# Revit family: A45743
name_source: partatom
category: Plumbing Fixtures
revit_build: Autodesk Revit 2017 (Build: 20160225_1515(x64)
units: mm (PartAtom-declared; Revit-internal decimal feet)

## family parameters
Cut with Voids When Loaded = No
Host = Face
OmniClass Number = 23.45.55.00
OmniClass Title = Sanitary Faucets, Wastes
Part Type = Normal
Room Calculation Point = No
Round Connector Dimension = Use Diameter
Shared = Yes

## types (1)
- ShowerHead-SlidingHandshowerSet-VitrA-BlissRailSeries-A45743EXP
    Article No. (default) = A45743EXP
    BIMobject category = Bath/Shower Mixer
    Brand = VitrA
    CW Connection = Yes
    Coating Material = Chrome
    Color = Chrome
    Connection Diameter (mm) = 15 mm  [stored 0.0492126 ft]
    Default Elevation = 850 mm
    Description = Bliss Rail Sliding Hand Shower Set
    Design country = Turkey
    Flow Rate(L/min. - 3 bar) = Max. 12L/min.
    HW Connection = Yes
    Hot Water Supply (max.) = 80 °C
    Hot Water temperature, factory set to = 38 °C
    IFC Classification = Sanitary Terminal
    Manufacturer = VitrA
    Manufacturer name = VitrA
    Masterformat 2014 Code = 22 41 23
    Masterformat 2014 Description = Residential Showers
    Min. flow pressure of = 0.5 bar
    Model = A45743EXP
    Mounting type = Wall Mounted
    NBS Referans Code = 35-06-81
    NBS Referans Description = Shower Heads
    Nominal Depth (mm) = 87 mm  [stored 0.285433 ft]
    Nominal Height (mm) = 680 mm  [stored 2.23097 ft]
    Nominal Width (mm) = 240 mm  [stored 0.787402 ft]
    Number Of Connections = 1
    OmniClass Code = 23-31 17 19
    OmniClass Description = Shower Head Fixtures
    Primary Material = Plastic1
    Product Properties = Sliding Hand Shower Set
    Product SKU = A45743EXP
    Product Type = Sliding Hand Shower Set
    Product certification = https://www.vitraglobal.com
    Product data url = https://www.vitra-bad.fr
    Product family = Shower System
    Product group = HandshowerSet
    Range of Hot Water Supply = 5 - 65 °C
    Range of flow pressure = 0.5-10 bar (Recommended 3-5 Bars)
    Secondary Material = Plastic
    Technical description = https://cdn.vitra.com.tr
    Test Pressure = 16 bar
    URL = https://vitraglobal.com
    Uniclass 1.4 Code = L7214
    Uniclass 1.4 Description = Showers
    Uniclass 2.0 Code = PR-35-06-81
    Uniclass 2.0 Description = Shower Heads
    Uniclass 2015 Code = Pr_40_20_87_76
    Uniclass 2015 Name = Shower heads
    Uniformat II Code = D2010
    Uniformat II Description = Plumbing Fixtures
    Vent Connection = No
    Warranty Period (Year) = 5 Years
    Waste Connection = No
    Weight Net (kg) = 1.31
    Youtube = https://www.youtube.com

note: [stored X ft] marks values corroborated as IEEE doubles in the binary element streams (Revit-internal decimal feet)

## geometry (parser evidence)
native form markers: Sweep x3
no freeform markers — native parametric forms only
